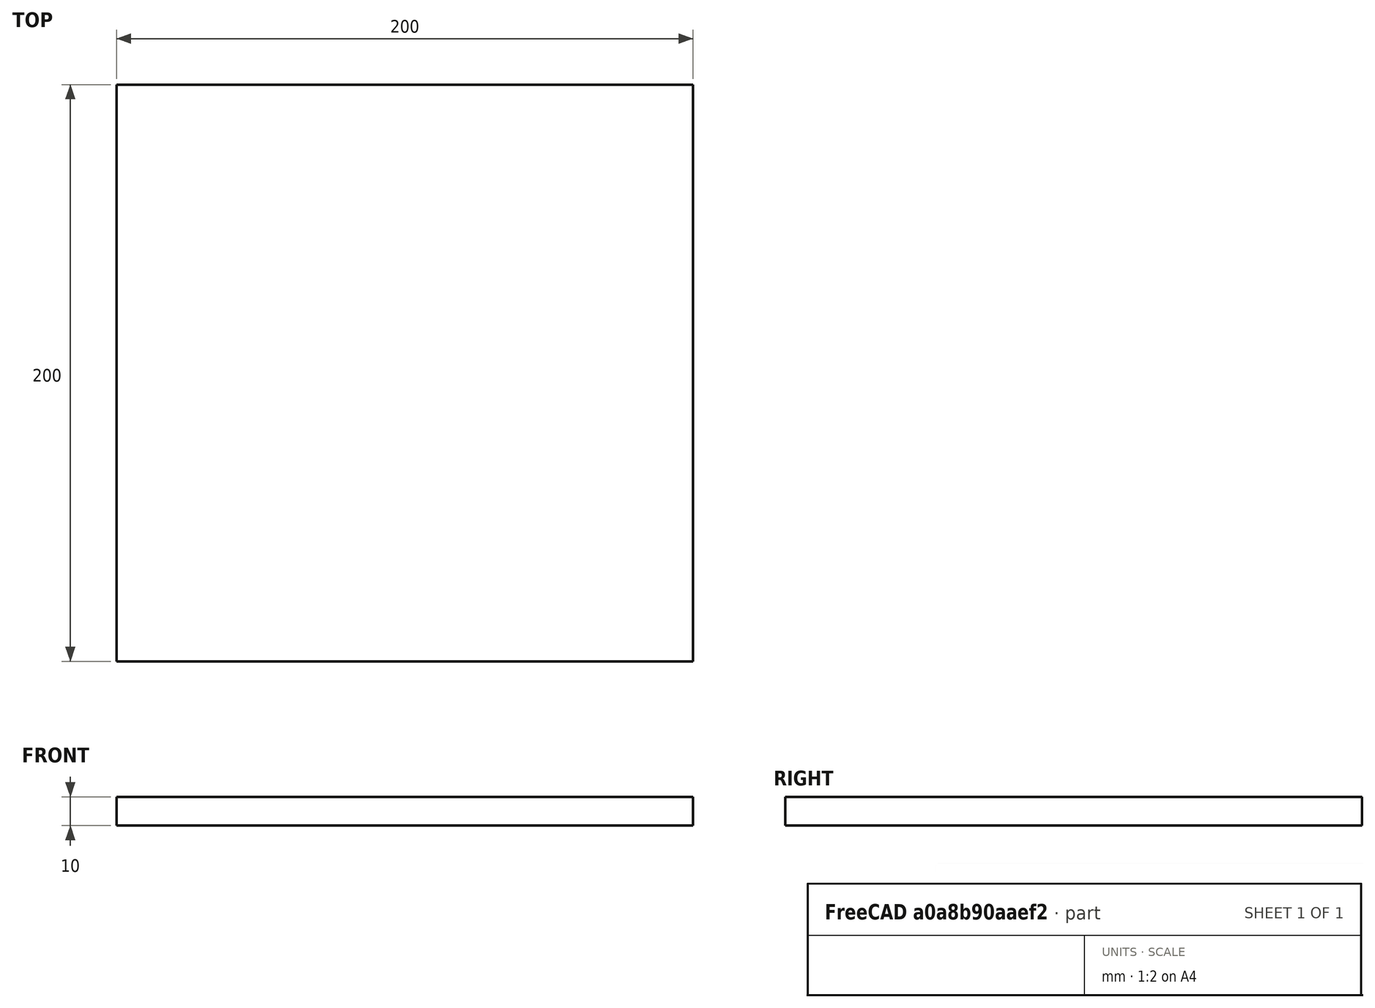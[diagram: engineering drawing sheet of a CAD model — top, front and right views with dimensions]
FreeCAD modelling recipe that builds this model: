
FCSTD DOCUMENT  (FreeCAD 0.19R)
Label: CAIXA-SCHROODINGER
License: All rights reserved
LicenseURL: http://en.wikipedia.org/wiki/All_rights_reserved
objects: Mesh::Feature×1, Spreadsheet::Sheet×1, Part::FeaturePython×1, Sketcher::SketchObject×1, Part::Extrusion×1
note: 3 computed .brp shape members not serialized (recipe doc carries the construction recipe); baked Part::Feature solids carry a one-line shape summary decoded from their .brp

FEATURE [Mesh::Feature] simonscat
  Placement = pos=(0,15,10) rot=(0,0,1;3.14159rad)
  expr: .Placement.Base.z = Spreadsheet.espessuragato
FEATURE [Spreadsheet::Sheet] Spreadsheet
  cells = A1=gato; C1(gato)=1; A2=altura; B2(altura)=20; C2(alturagato)==10 * gato * altura; A3=largura; B3(largura)=20; C3(larguragato)==10 * gato * largura; A4=comprimento; B4(comprimento)=20; C4(comprimentogato)==10 * gato * comprimento; A5=espessura; B5(espessura)==altura / 20; C5(espessuragato)==10 * gato * espessura
FEATURE [Part::FeaturePython] Clone  label="simonscat001"  # Draft clone (typed FeaturePython)
  AttacherType = Attacher::AttachEngine3D
  Fuse = false
  Objects = -> [simonscat]
  Placement = pos=(0,15,0) rot=(0,0,1;3.14159rad)
  Scale = (1,1,1)
  expr: .Scale.z = Spreadsheet.gato
  expr: .Scale.y = Spreadsheet.gato
  expr: .Scale.x = Spreadsheet.gato
FEATURE [Sketcher::SketchObject] Sketch
  expr: Constraints[9] = Spreadsheet.alturagato
  expr: Constraints[8] = Spreadsheet.larguragato
  sketch-geometry (4):
    g0: LineSegment StartX=-109.641 StartY=95.2681 StartZ=0 EndX=90.3586 EndY=95.2681 EndZ=0
    g1: LineSegment StartX=90.3586 StartY=95.2681 StartZ=0 EndX=90.3586 EndY=-104.732 EndZ=0
    g2: LineSegment StartX=90.3586 StartY=-104.732 StartZ=0 EndX=-109.641 EndY=-104.732 EndZ=0
    g3: LineSegment StartX=-109.641 StartY=-104.732 StartZ=0 EndX=-109.641 EndY=95.2681 EndZ=0
  constraints (10):
    c: Coincident(g0,g1)
    c: Coincident(g1,g2)
    c: Coincident(g2,g3)
    c: Coincident(g3,g0)
    c: Horizontal(g0)
    c: Horizontal(g2)
    c: Vertical(g1)
    c: Vertical(g3)
    c: DistanceX(g0,g0) = 200
    c: DistanceY(g3,g3) = 200
FEATURE [Part::Extrusion] Extrude
  Base = -> Sketch
  Dir = (0,0,1)
  DirMode = 2
  FaceMakerClass = Part::FaceMakerBullseye
  LengthFwd = 10
  LengthRev = 0
  Solid = true
  Symmetric = false
  expr: LengthFwd = Spreadsheet.espessuragato
